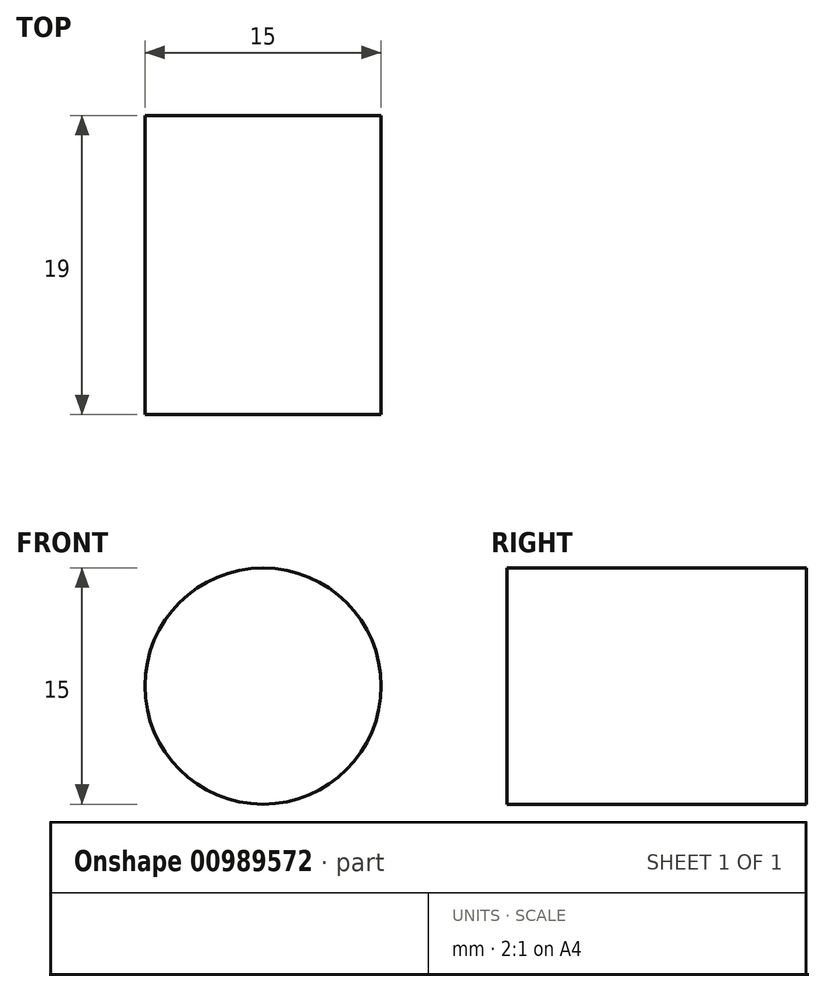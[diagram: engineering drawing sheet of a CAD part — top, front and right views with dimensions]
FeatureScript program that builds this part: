
annotation { "Feature Type Name" : "Feature", "Feature Type Description" : "" }
export const myFeature = defineFeature(function(context is Context, id is Id, definition is map)
    precondition{}
    {
        {
            var Q0;
            Q0=qCreatedBy(makeId("Front.planeOp"),FACE);
            var sketch = newSketch(context, id + "F0", { "sketchPlane" : qUnion([Q0])});
            skCircle(sketch, "E0", {"center": v(0, 0) * mm, "radius": 7.5 * mm});
            skSolve(sketch);
        }
        {
            var Q0;
            Q0 = qSketchRegion(id + "F0", true);
            extrude(context, id + "F1", {"entities" : qUnion([Q0]), "oppositeDirection" : true, "depth" : 19 * mm, "offsetDistance" : 25 * mm});
        }
    });
